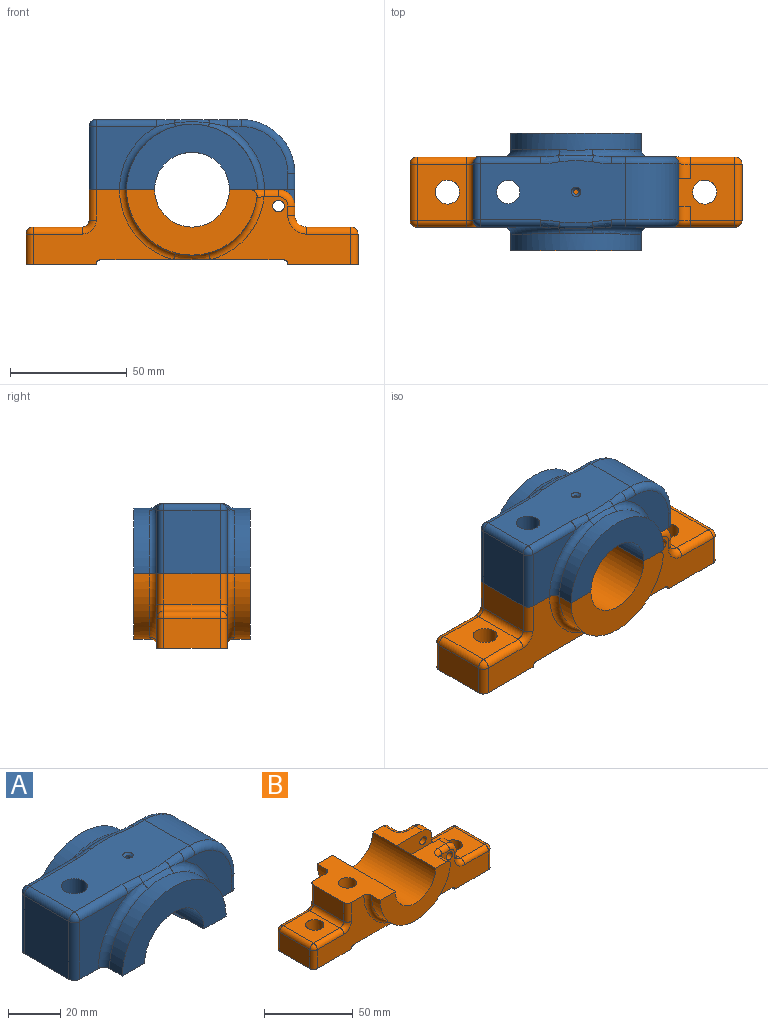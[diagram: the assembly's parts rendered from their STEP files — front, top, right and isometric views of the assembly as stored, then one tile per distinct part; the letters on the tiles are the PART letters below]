
ASSEMBLY  parts=2 mates=1
PART A: 51 faces, bbox 89.9x50x48.7 mm
  f0: plane 27x25.77mm, normal (0,1,0), area 307.6mm2, adj f11,f32,f42,f43,f44
  f1: plane 27x25.77mm, normal (0,-1,0), area 393.4mm2, adj f3,f27,f39,f41
  f2: cylinder r=16mm len=50mm, axis (0,-1,0), area 2510.1mm2, adj f3,f4,f5,f11,f15,f18,f22
  f3: plane 50x28mm, normal (0,0,-1), area 926.1mm2, adj f1,f2,f10,f12,f15,f16,f17,f18
  f4: plane 28x19mm, normal (0,0,-1), area 372mm2, adj f2,f7,f8,f14,f17,f18,f29,f33
  f5: cylinder r=30mm len=19.58mm, axis (0,1,0), area 296.1mm2, adj f2,f6,f13,f14
  f6: cylinder r=7mm len=12mm, axis (0,1,0), area 149.1mm2, adj f5,f8,f13,f14
  f7: plane 27x25.77mm, normal (0,-1,0), area 307.6mm2, adj f4,f29,f33,f34,f35
  f8: plane 24x14mm, normal (1,0,0), area 252mm2, adj f4,f6,f11,f13,f14,f25,f33,f42
  f9: plane 62x26.72mm, normal (0,0,1), area 1441.3mm2, adj f21,f23,f25,f26,f35,f36,f37,f38
  f10: plane 27x24mm, normal (-1,0,0), area 648mm2, adj f3,f26,f41,f50
  f11: plane 28x19mm, normal (0,0,-1), area 372mm2, adj f0,f2,f8,f13,f15,f16,f32,f42
  f12: plane 27x25.77mm, normal (0,1,0), area 393.4mm2, adj f3,f30,f48,f50
  f13: plane 28x14mm, normal (0,1,0), area 263.6mm2, adj f5,f6,f8,f11,f24
  f14: plane 28x14mm, normal (0,-1,0), area 263.6mm2, adj f4,f5,f6,f8,f24
  f15: plane 56x28mm, normal (0,1,0), area 829.4mm2, adj f2,f3,f11,f16
  f16: cylinder r=28mm len=56mm, axis (0,1,0), area 615.8mm2, adj f3,f11,f15,f30,f31,f32
  f17: cylinder r=28mm len=56mm, axis (0,1,0), area 615.8mm2, adj f3,f4,f18,f27,f28,f29
  f18: plane 56x28mm, normal (0,-1,0), area 829.4mm2, adj f2,f3,f4,f17
  f19: cylinder r=7mm len=20mm, axis (0,0,1), area 879.6mm2, adj f3,f20
  f20: cone r=5mm half-angle=59deg, axis (0,0,-1), area 87.9mm2, adj f19,f21
  f21: cylinder r=5mm len=10mm, axis (0,0,1), area 276.5mm2, adj f9,f20
  f22: cylinder r=1mm len=13.03mm, axis (0,0,1), area 81.9mm2, adj f2,f23
  f23: cone r=1mm half-angle=45deg, axis (0,0,1), area 13.3mm2, adj f9,f22
  f24: cylinder r=2.5mm len=12mm, axis (0,-1,0), area 188.5mm2, adj f13,f14
  f25: cylinder r=23mm len=24mm, axis (0,1,0), area 867.1mm2, adj f8,f9,f34,f43
  f26: cylinder r=3mm len=24mm, axis (0,1,0), area 113.1mm2, adj f9,f10,f40,f49
  f27: torus R=31mm, axis (0,-1,0), area 174mm2, adj f1,f3,f17,f28,f38
  f28: bspline ~16.86x3.21mm, area 38.1mm2, adj f17,f27,f29,f37
  f29: torus R=31mm, axis (0,-1,0), area 174mm2, adj f4,f7,f17,f28,f36
  f30: torus R=31mm, axis (0,-1,0), area 174mm2, adj f3,f12,f16,f31,f47
  f31: bspline ~16.86x3.21mm, area 38.1mm2, adj f16,f30,f32,f46
  f32: torus R=31mm, axis (0,-1,0), area 174mm2, adj f0,f11,f16,f31,f45
  f33: cylinder r=3mm len=7mm, axis (0,0,-1), area 33mm2, adj f4,f7,f8,f34
  f34: torus R=20mm, axis (0,-1,0), area 162.2mm2, adj f7,f25,f33,f35
  f35: cylinder r=3mm len=5.77mm, axis (1,0,0), area 27.2mm2, adj f7,f9,f34,f36
  f36: bspline ~9.92x3.47mm, area 31mm2, adj f9,f29,f35,f37
  f37: bspline ~17.02x2.9mm, area 39.6mm2, adj f9,f28,f36,f38
  f38: bspline ~10.65x3.53mm, area 31mm2, adj f9,f27,f37,f39
  f39: cylinder r=3mm len=25.77mm, axis (1,0,0), area 121.4mm2, adj f1,f9,f38,f40
  f40: sphere r=3mm, area 14.1mm2, adj f26,f39,f41
  f41: cylinder r=3mm len=27mm, axis (0,0,1), area 127.2mm2, adj f1,f3,f10,f40
  f42: cylinder r=3mm len=7mm, axis (0,0,1), area 33mm2, adj f0,f8,f11,f43
  f43: torus R=20mm, axis (0,-1,0), area 162.2mm2, adj f0,f25,f42,f44
  f44: cylinder r=3mm len=5.77mm, axis (-1,0,0), area 27.2mm2, adj f0,f9,f43,f45
  f45: bspline ~9.92x3.47mm, area 31mm2, adj f9,f32,f44,f46
  f46: bspline ~17.02x2.9mm, area 39.6mm2, adj f9,f31,f45,f47
  f47: bspline ~11.86x3.55mm, area 31mm2, adj f9,f30,f46,f48
  f48: cylinder r=3mm len=25.77mm, axis (-1,0,0), area 121.4mm2, adj f9,f12,f47,f49
  f49: sphere r=3mm, area 14.1mm2, adj f26,f48,f50
  f50: cylinder r=3mm len=27mm, axis (0,0,-1), area 127.2mm2, adj f3,f10,f12,f49
PART B: 73 faces, bbox 142.1x50.1x35.3 mm
  f0: plane 60.19x32mm, normal (0,1,0), area 840mm2, adj f6,f7,f12,f30,f42,f68,f69,f70
  f1: plane 60.19x29mm, normal (0,-1,0), area 792.8mm2, adj f7,f8,f26,f31,f41,f54,f56,f57
  f2: plane 21x19mm, normal (0,0,1), area 248.4mm2, adj f18,f22,f28,f37,f51,f52,f53
  f3: plane 6x4mm, normal (1,0,0), area 24mm2, adj f28,f35,f37,f49
  f4: cylinder r=2.5mm len=9mm, axis (0,-1,0), area 141.4mm2, adj f17,f28
  f5: plane 21x19mm, normal (0,0,1), area 248.4mm2, adj f21,f22,f29,f38,f60,f61,f62
  f6: plane 30x30mm, normal (0,0,-1), area 812.8mm2, adj f0,f15,f16,f23,f30,f67,f72
  f7: plane 78.07x30.07mm, normal (0,0,-1), area 2256.7mm2, adj f0,f1,f16,f17,f25,f30,f31,f40
  f8: plane 30x30mm, normal (0,0,-1), area 812.8mm2, adj f1,f9,f17,f24,f31,f45,f54
  f9: plane 24x13mm, normal (1,0,0), area 312mm2, adj f8,f32,f45,f54
  f10: plane 24.87x24mm, normal (0,0,1), area 443.1mm2, adj f24,f27,f28,f29,f32,f35,f36,f47
  f11: plane 6x4mm, normal (1,0,0), area 24mm2, adj f29,f36,f38,f58
  f12: plane 50x28mm, normal (0,0,1), area 996.7mm2, adj f0,f13,f16,f18,f19,f20,f21,f22
  f13: plane 24x13mm, normal (-1,0,0), area 312mm2, adj f12,f33,f63,f68
  f14: plane 24x21mm, normal (0,0,1), area 420.7mm2, adj f23,f33,f34,f65,f70
  f15: plane 24x13mm, normal (-1,0,0), area 312mm2, adj f6,f34,f67,f72
  f16: plane 60.19x32mm, normal (0,-1,0), area 840mm2, adj f6,f7,f12,f30,f39,f63,f64,f65
  f17: plane 60.19x29mm, normal (0,1,0), area 792.8mm2, adj f4,f7,f8,f31,f44,f45,f47,f48
  f18: plane 55.82x28mm, normal (0,1,0), area 827.1mm2, adj f2,f12,f19,f22,f53
  f19: cylinder r=28mm len=55.8mm, axis (0,1,0), area 592.2mm2, adj f12,f18,f42,f43,f44,f53
  f20: cylinder r=28mm len=55.8mm, axis (0,1,0), area 592.2mm2, adj f12,f21,f39,f40,f41,f62
  f21: plane 55.82x28mm, normal (0,-1,0), area 827.1mm2, adj f5,f12,f20,f22,f62
  f22: cylinder r=16mm len=50mm, axis (0,-1,0), area 2513.3mm2, adj f2,f5,f12,f18,f21,f27
  f23: cylinder r=5.15mm len=16mm, axis (0,0,1), area 517.7mm2, adj f6,f14
  f24: cylinder r=5.15mm len=16mm, axis (0,0,1), area 517.7mm2, adj f8,f10
  f25: cylinder r=5.15mm len=30mm, axis (0,0,1), area 970.8mm2, adj f7,f12
  f26: cylinder r=2.5mm len=9mm, axis (0,-1,0), area 141.4mm2, adj f1,f29
  f27: cylinder r=31mm len=27.13mm, axis (0,-1,0), area 396.4mm2, adj f10,f22,f28,f29
  f28: plane 33x16mm, normal (0,-1,0), area 297.8mm2, adj f2,f3,f4,f10,f27,f35,f37
  f29: plane 33x16mm, normal (0,1,0), area 297.8mm2, adj f5,f10,f11,f26,f27,f36,f38
  f30: cylinder r=2mm len=30mm, axis (0,-1,0), area 94.2mm2, adj f0,f6,f7,f16
  f31: cylinder r=2mm len=30mm, axis (0,-1,0), area 94.2mm2, adj f1,f7,f8,f17
  f32: cylinder r=3mm len=24mm, axis (0,1,0), area 113.1mm2, adj f9,f10,f46,f55
  f33: cylinder r=3mm len=24mm, axis (0,-1,0), area 113.1mm2, adj f13,f14,f64,f69
  f34: cylinder r=3mm len=24mm, axis (0,1,0), area 113.1mm2, adj f14,f15,f66,f71
  f35: cylinder r=5mm len=6mm, axis (0,-1,0), area 47.1mm2, adj f3,f10,f28,f48
  f36: cylinder r=5mm len=6mm, axis (0,-1,0), area 47.1mm2, adj f10,f11,f29,f57
  f37: cylinder r=7mm len=7mm, axis (0,1,0), area 66mm2, adj f2,f3,f28,f50
  f38: cylinder r=7mm len=7mm, axis (0,1,0), area 66mm2, adj f5,f11,f29,f59
  f39: torus R=31mm, axis (0,-1,0), area 180.4mm2, adj f12,f16,f20,f40
  f40: bspline ~16.86x3.21mm, area 59.3mm2, adj f7,f20,f39,f41
  f41: torus R=31mm, axis (0,-1,0), area 165.6mm2, adj f1,f20,f40,f61
  f42: torus R=31mm, axis (0,-1,0), area 180.4mm2, adj f0,f12,f19,f43
  f43: bspline ~16.86x3.21mm, area 59.3mm2, adj f7,f19,f42,f44
  f44: torus R=31mm, axis (0,-1,0), area 165.6mm2, adj f17,f19,f43,f52
  f45: cylinder r=3mm len=13mm, axis (0,0,1), area 61.3mm2, adj f8,f9,f17,f46
  f46: sphere r=3mm, area 14.1mm2, adj f32,f45,f47
  f47: cylinder r=3mm len=19mm, axis (-1,0,0), area 89.5mm2, adj f10,f17,f46,f48
  f48: torus R=8mm, axis (0,-1,0), area 45.1mm2, adj f17,f35,f47,f49
  f49: cylinder r=3mm len=4mm, axis (0,0,1), area 18.8mm2, adj f3,f17,f48,f50
  f50: torus R=4mm, axis (0,-1,0), area 43.7mm2, adj f17,f37,f49,f51
  f51: cylinder r=3mm len=6.15mm, axis (-1,0,0), area 29mm2, adj f2,f17,f50,f52
  f52: bspline ~7.33x6.38mm, area 31.4mm2, adj f2,f44,f51,f53
  f53: cylinder r=3mm len=7mm, axis (0,1,0), area 35.5mm2, adj f2,f18,f19,f52
  f54: cylinder r=3mm len=13mm, axis (0,0,-1), area 61.3mm2, adj f1,f8,f9,f55
  f55: sphere r=3mm, area 14.1mm2, adj f32,f54,f56
  f56: cylinder r=3mm len=19mm, axis (1,0,0), area 89.5mm2, adj f1,f10,f55,f57
  f57: torus R=8mm, axis (0,-1,0), area 45.1mm2, adj f1,f36,f56,f58
  f58: cylinder r=3mm len=4mm, axis (0,0,-1), area 18.8mm2, adj f1,f11,f57,f59
  f59: torus R=4mm, axis (0,-1,0), area 43.7mm2, adj f1,f38,f58,f60
  f60: cylinder r=3mm len=6.15mm, axis (1,0,0), area 29mm2, adj f1,f5,f59,f61
  f61: bspline ~7.38x7.33mm, area 31.4mm2, adj f5,f41,f60,f62
  f62: cylinder r=3mm len=7mm, axis (0,1,0), area 35.5mm2, adj f5,f20,f21,f61
  f63: cylinder r=3mm len=13mm, axis (0,0,1), area 61.3mm2, adj f12,f13,f16,f64
  f64: torus R=6mm, axis (0,-1,0), area 30.3mm2, adj f16,f33,f63,f65
  f65: cylinder r=3mm len=21mm, axis (1,0,0), area 99mm2, adj f14,f16,f64,f66
  f66: sphere r=3mm, area 14.1mm2, adj f34,f65,f67
  f67: cylinder r=3mm len=13mm, axis (0,0,1), area 61.3mm2, adj f6,f15,f16,f66
  f68: cylinder r=3mm len=13mm, axis (0,0,-1), area 61.3mm2, adj f0,f12,f13,f69
  f69: torus R=6mm, axis (0,-1,0), area 30.3mm2, adj f0,f33,f68,f70
  f70: cylinder r=3mm len=21mm, axis (-1,0,0), area 99mm2, adj f0,f14,f69,f71
  f71: sphere r=3mm, area 14.1mm2, adj f34,f70,f72
  f72: cylinder r=3mm len=13mm, axis (0,0,-1), area 61.3mm2, adj f0,f6,f15,f71
PLACE A t=(0,0,32)mm
PLACE B at identity fixed
MATE fastened A.f2 <-> B.f19  axis (0,-1,0) through (0,-25,32)mm
